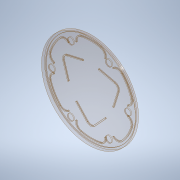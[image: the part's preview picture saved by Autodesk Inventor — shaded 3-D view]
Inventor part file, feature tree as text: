
AUTODESK INVENTOR PART (.ipt)
format: ipt  version: 2020 (Build 240168000, 168)  size: 408,576 bytes
history: native  units: in
note: dims shown in document units (in); Inventor stores cm internally (conversion verified against a paired STEP export)
features: sketch x14, extrude x11, projected_geometry x6, plane x2, shell x1, sweep x1, hole x1
ambient origin geometry x8: Origin, YZ Plane, XZ Plane, XY Plane, X Axis, Y Axis, Z Axis, Center Point
bodies: Solid1 (feature_tree)
feature tree (36):
  extrude  "Extrusion1"  Depth=3.1496in TaperAngle=0.0deg
  shell  "Shell1"  Thickness=0.1181in
  extrude  "Extrusion2"  Depth=3.1496in TaperAngle=0.0deg
  extrude  "Extrusion3"  Depth=1.5748in
  plane  "Work Plane1"
  extrude  "Extrusion4"  TaperAngle=120.0deg  [1 undecoded]
  extrude  "Extrusion5"  Depth=0.378in
  plane  "Work Plane4"
  sweep  "Sweep2"
  extrude  "Extrusion6"  [1 undecoded]
  hole  "Hole1"  [1 undecoded]
  extrude  "Extrusion9"  Depth=0.1181in TaperAngle=0.0deg
  extrude  "Extrusion10"  Depth=0.0591in
  extrude  "Extrusion11"  Depth=0.0591in
  extrude  "Extrusion13"  Depth=0.0591in
  extrude  "Extrusion12"  Depth=0.0591in
  sketch  "Sketch1"  dims[d1=5.3543in d2=3.1496in d3=0.0in d4=0.1181in]
  sketch  "Sketch2"  dims[d5=2.5197in d6=3.1496in d7=0.0in]
  sketch  "Sketch3"  dims[d8=0.378in d9=1.5748in]
  projected_geometry  "Projected Loop1"
  sketch  "Sketch4"  dims[d10=120.0deg d11=120.0deg]
  sketch  "Sketch6"  dims[d12=0.378in d13=0.378in]
  projected_geometry  "Projected Loop3"
  sketch  "Sketch9"  dims[d14=1.5748in d15=1.5748in]
  projected_geometry  "Projected Loop4"
  sketch  "Sketch10"  dims[d16=0.06in d17=0.0in d18=-0.9843in]
  sketch  "Sketch11"  dims[d24=1.1811in d25=0.9843in d26=0.0in]
  projected_geometry  "Projected Loop5"
  sketch  "Sketch14"  dims[d27=0.1181in d28=2.2201in d29=0.0in]
  sketch  "Sketch16"  dims[d37=0.0in d38=0.0in d39=0.0591in]
  sketch  "Sketch17"  dims[d40=0.0591in d41=0.0591in]
  projected_geometry  "Projected Loop7"
  sketch  "Sketch18"  dims[d42=0.0591in d43=0.0591in]
  sketch  "Sketch19"  dims[d44=0.0591in d45=0.0591in]
  sketch  "Sketch20"  dims[d46=0.9843in d47=0.9843in d48=0.9843in d49=0.9843in d50=0.9843in d51=0.9843in d52=0.0591in d53=0.0in d98=0.2362in d99=1.6142in d100=1.1811in d102=360.0deg d104=0.2362in d105=0.2362in d106=0.1575in d107=0.0787in d108=90.0deg d109=0.315in d110=0.8108in d111=0.3937in d112=0.0in d113=0.3937in d114=0.0in d115=5.5906in d116=0.378in d117=5.1181in d118=2.2638in d119=0.0591in d120=0.7874in d121=0.7874in d122=2.3622in d124=360.0deg d126=0.0591in d127=0.0591in d128=2.3622in d130=360.0deg d132=0.0591in d133=0.0in d134=0.378in d135=2.2638in d136=2.3622in d138=360.0deg d140=0.06in d141=0.0in d142=0.0591in d143=0.0in]
  projected_geometry  "Projected Loop8"
note: 3 required parameter values undecoded (feature->parameter linkage not recoverable at this tier; creation-order binding heuristic only, values carry confidence <= 0.55)
